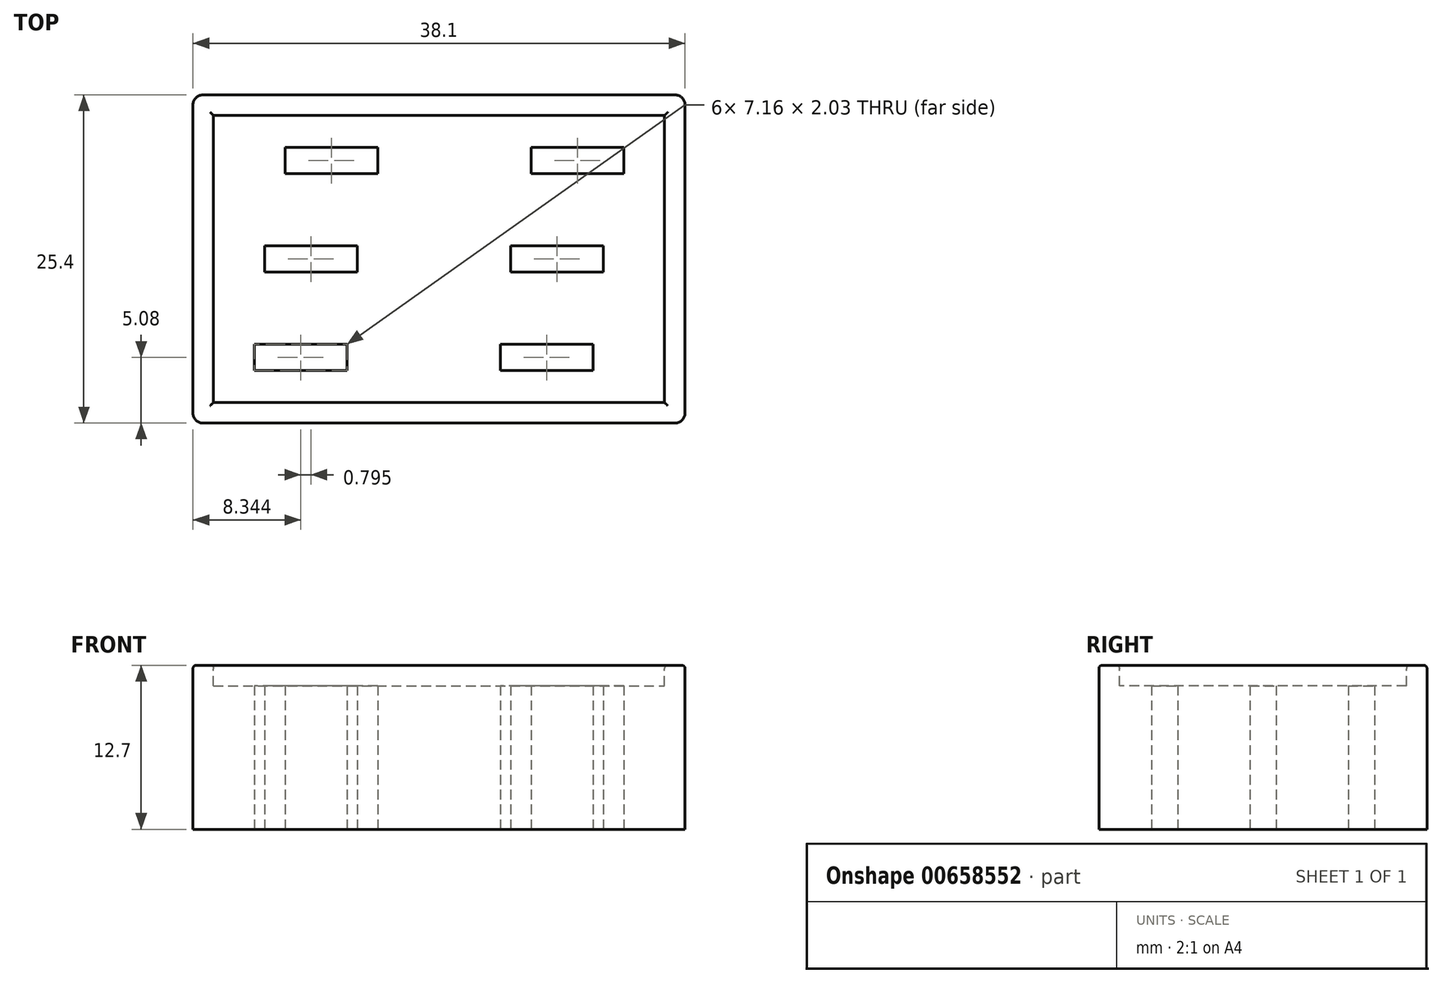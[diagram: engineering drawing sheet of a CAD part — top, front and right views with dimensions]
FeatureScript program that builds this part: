
annotation { "Feature Type Name" : "Feature", "Feature Type Description" : "" }
export const myFeature = defineFeature(function(context is Context, id is Id, definition is map)
    precondition{}
    {
        {
            var Q0;
            Q0=qCreatedBy(makeId("Top.planeOp"),FACE);
            var sketch = newSketch(context, id + "F0", { "sketchPlane" : qUnion([Q0])});
            skLineSegment(sketch, "E0.bottom", {"start": v(-19.05, 12.7) * mm, "end": v(19.05, 12.7) * mm});
            skLineSegment(sketch, "E0.top", {"start": v(-19.05, -12.7) * mm, "end": v(19.05, -12.7) * mm});
            skLineSegment(sketch, "E0.left", {"start": v(-19.05, 12.7) * mm, "end": v(-19.05, -12.7) * mm});
            skLineSegment(sketch, "E0.right", {"start": v(19.05, 12.7) * mm, "end": v(19.05, -12.7) * mm});
            skSolve(sketch);
        }
        {
            var Q0;
            Q0 = qSketchRegion(id + "F0", true);
            extrude(context, id + "F1", {"entities" : qUnion([Q0]), "depth" : 12.7 * mm, "offsetDistance" : 25.4 * mm});
        }
        {
            var Q0;
            Q0=makeQuery(id+"F1.opExtrude","CAP_FACE",FACE,{"disambiguationData":[OSD([sQuery(id+"F0.wireOp",EDGE,"E0.bottom"),sQuery(id+"F0.wireOp",EDGE,"E0.top"),sQuery(id+"F0.wireOp",EDGE,"E0.left"),sQuery(id+"F0.wireOp",EDGE,"E0.right")])],"isStart":false});
            var sketch = newSketch(context, id + "F2", { "sketchPlane" : qUnion([Q0])});
            skLineSegment(sketch, "E1.bottom", {"start": v(-17.46, 11.11) * mm, "end": v(17.46, 11.11) * mm});
            skLineSegment(sketch, "E1.top", {"start": v(-17.46, -11.11) * mm, "end": v(17.46, -11.11) * mm});
            skLineSegment(sketch, "E1.left", {"start": v(-17.46, 11.11) * mm, "end": v(-17.46, -11.11) * mm});
            skLineSegment(sketch, "E1.right", {"start": v(17.46, 11.11) * mm, "end": v(17.46, -11.11) * mm});
            skSolve(sketch);
        }
        {
            var Q0;
            Q0 = qSketchRegion(id + "F2", true);
            extrude(context, id + "F3", {"entities" : qUnion([Q0]), "operationType" : NewBodyOperationType.REMOVE, "oppositeDirection" : true, "depth" : 1.59 * mm, "offsetDistance" : 25.4 * mm});
        }
        {
            var Q0;
            Q0=makeQuery(id+"F1.opExtrude","SWEPT_EDGE",EDGE,{"disambiguationData":[OSD([sQuery(id+"F0.wireOp",EDGE,"E0.top"),sQuery(id+"F0.wireOp",EDGE,"E0.left")])]});
            var Q1;
            Q1=makeQuery(id+"F1.opExtrude","SWEPT_EDGE",EDGE,{"disambiguationData":[OSD([sQuery(id+"F0.wireOp",EDGE,"E0.bottom"),sQuery(id+"F0.wireOp",EDGE,"E0.left")])]});
            var Q2;
            Q2=makeQuery(id+"F1.opExtrude","SWEPT_EDGE",EDGE,{"disambiguationData":[OSD([sQuery(id+"F0.wireOp",EDGE,"E0.bottom"),sQuery(id+"F0.wireOp",EDGE,"E0.right")])]});
            var Q3;
            Q3=makeQuery(id+"F1.opExtrude","SWEPT_EDGE",EDGE,{"disambiguationData":[OSD([sQuery(id+"F0.wireOp",EDGE,"E0.top"),sQuery(id+"F0.wireOp",EDGE,"E0.right")])]});
            fillet(context, id + "F4", {"entities" : qUnion([Q0, Q1, Q2, Q3]), "radius" : 0.76 * mm, "tangentPropagation" : true, "allowEdgeOverflow" : false});
        }
        {
            var Q0;
            Q0=makeQuery(id+"F1.opExtrude","CAP_FACE",FACE,{"disambiguationData":[OSD([sQuery(id+"F0.wireOp",EDGE,"E0.bottom"),sQuery(id+"F0.wireOp",EDGE,"E0.top"),sQuery(id+"F0.wireOp",EDGE,"E0.left"),sQuery(id+"F0.wireOp",EDGE,"E0.right")])],"isStart":false});
            fillet(context, id + "F5", {"entities" : qUnion([Q0]), "radius" : 0.25 * mm, "tangentPropagation" : true, "allowEdgeOverflow" : false});
        }
        {
            var Q0;
            Q0=qCreatedBy(makeId("Top.planeOp"),FACE);
            var sketch = newSketch(context, id + "F6", { "sketchPlane" : qUnion([Q0])});
            skLineSegment(sketch, "E2.bottom", {"start": v(-14.29, -6.6) * mm, "end": v(-7.12, -6.6) * mm});
            skLineSegment(sketch, "E2.top", {"start": v(-14.29, -8.64) * mm, "end": v(-7.12, -8.64) * mm});
            skLineSegment(sketch, "E2.left", {"start": v(-14.29, -6.6) * mm, "end": v(-14.29, -8.64) * mm});
            skLineSegment(sketch, "E2.right", {"start": v(-7.12, -6.6) * mm, "end": v(-7.12, -8.64) * mm});
            skLineSegment(sketch, "E3.bottom", {"start": v(-13.5, 1.02) * mm, "end": v(-6.33, 1.02) * mm});
            skLineSegment(sketch, "E3.top", {"start": v(-13.5, -1.02) * mm, "end": v(-6.33, -1.02) * mm});
            skLineSegment(sketch, "E3.left", {"start": v(-13.5, 1.02) * mm, "end": v(-13.5, -1.02) * mm});
            skLineSegment(sketch, "E3.right", {"start": v(-6.33, 1.02) * mm, "end": v(-6.33, -1.02) * mm});
            skLineSegment(sketch, "E4.bottom", {"start": v(-11.9, 8.64) * mm, "end": v(-4.74, 8.64) * mm});
            skLineSegment(sketch, "E4.top", {"start": v(-11.9, 6.6) * mm, "end": v(-4.74, 6.6) * mm});
            skLineSegment(sketch, "E4.left", {"start": v(-11.9, 8.64) * mm, "end": v(-11.9, 6.6) * mm});
            skLineSegment(sketch, "E4.right", {"start": v(-4.74, 8.64) * mm, "end": v(-4.74, 6.6) * mm});
            skLineSegment(sketch, "E5.1.0.0", {"start": v(5.56, 1.02) * mm, "end": v(5.56, -1.02) * mm});
            skLineSegment(sketch, "E5.1.0.1", {"start": v(4.76, -6.6) * mm, "end": v(11.93, -6.6) * mm});
            skLineSegment(sketch, "E5.1.0.2", {"start": v(14.3, 8.64) * mm, "end": v(14.3, 6.6) * mm});
            skLineSegment(sketch, "E5.1.0.3", {"start": v(7.15, 8.64) * mm, "end": v(7.15, 6.6) * mm});
            skLineSegment(sketch, "E5.1.0.4", {"start": v(7.15, 6.6) * mm, "end": v(14.3, 6.6) * mm});
            skLineSegment(sketch, "E5.1.0.5", {"start": v(7.15, 8.64) * mm, "end": v(14.3, 8.64) * mm});
            skLineSegment(sketch, "E5.1.0.6", {"start": v(5.56, -1.02) * mm, "end": v(12.72, -1.02) * mm});
            skLineSegment(sketch, "E5.1.0.7", {"start": v(5.56, 1.02) * mm, "end": v(12.72, 1.02) * mm});
            skLineSegment(sketch, "E5.1.0.8", {"start": v(11.93, -6.6) * mm, "end": v(11.93, -8.64) * mm});
            skLineSegment(sketch, "E5.1.0.9", {"start": v(12.72, 1.02) * mm, "end": v(12.72, -1.02) * mm});
            skLineSegment(sketch, "E5.1.0.10", {"start": v(4.76, -6.6) * mm, "end": v(4.76, -8.64) * mm});
            skLineSegment(sketch, "E5.1.0.11", {"start": v(4.76, -8.64) * mm, "end": v(11.93, -8.64) * mm});
            skLineSegment(sketch, "E5.direction1", {"start": v(-14.29, -8.64) * mm, "end": v(4.76, -8.64) * mm, "construction": true});
            skSolve(sketch);
        }
        {
            var Q0;
            Q0 = qSketchRegion(id + "F6", true);
            extrude(context, id + "F7", {"entities" : qUnion([Q0]), "operationType" : NewBodyOperationType.REMOVE, "depth" : 25.4 * mm, "offsetDistance" : 25.4 * mm});
        }
    });
